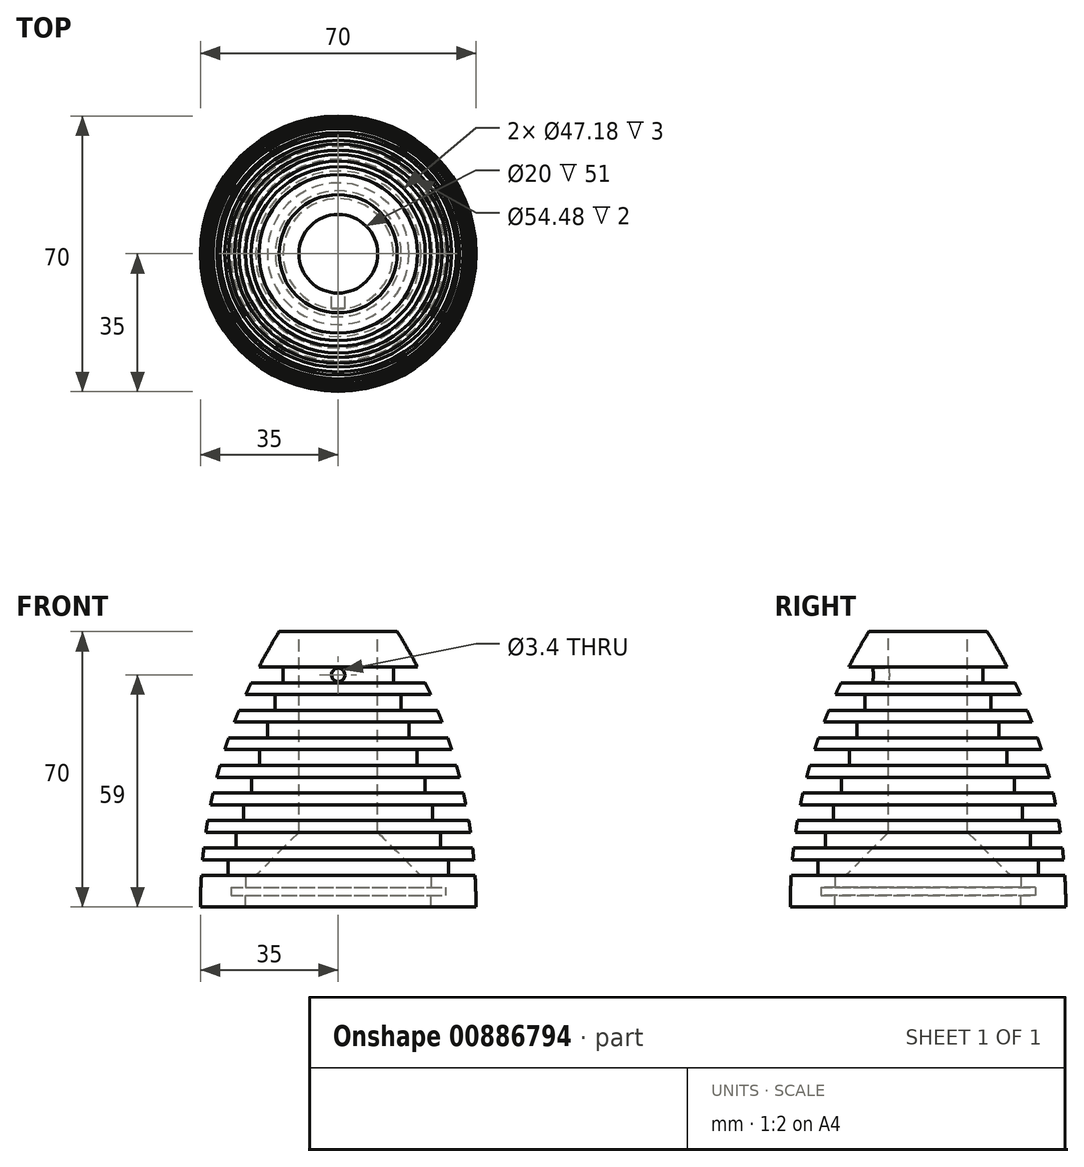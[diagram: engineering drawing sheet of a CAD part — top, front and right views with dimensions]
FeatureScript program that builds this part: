
annotation { "Feature Type Name" : "Feature", "Feature Type Description" : "" }
export const myFeature = defineFeature(function(context is Context, id is Id, definition is map)
    precondition{}
    {
        {
            var Q0;
            Q0=qCreatedBy(makeId("Front.planeOp"),FACE);
            var sketch = newSketch(context, id + "F0", { "sketchPlane" : qUnion([Q0])});
            skLineSegment(sketch, "E0", {"start": v(-35, -70) * mm, "end": v(-23.55, -70) * mm});
            skLineSegment(sketch, "E1", {"start": v(0, -70) * mm, "end": v(0, 0) * mm});
            skLineSegment(sketch, "E2", {"start": v(0, 0) * mm, "end": v(-15, 0) * mm});
            skArc(sketch, "E3", {"start": v(-15, 0) * mm, "mid": v(-17.65, -4.45) * mm, "end": v(-20.12, -9) * mm});
            skLineSegment(sketch, "E4", {"start": v(-23.5, -16) * mm, "end": v(-16, -16) * mm});
            skLineSegment(sketch, "E5", {"start": v(-16, -16) * mm, "end": v(-16, -20) * mm});
            skLineSegment(sketch, "E6", {"start": v(-16, -20) * mm, "end": v(-25.2, -20) * mm});
            skLineSegment(sketch, "E7", {"start": v(-26.38, -23) * mm, "end": v(-18, -23) * mm});
            skLineSegment(sketch, "E8", {"start": v(-18, -23) * mm, "end": v(-18, -27) * mm});
            skLineSegment(sketch, "E9", {"start": v(-18, -27) * mm, "end": v(-27.83, -27) * mm});
            skLineSegment(sketch, "E10", {"start": v(-28.82, -30) * mm, "end": v(-20, -30) * mm});
            skLineSegment(sketch, "E11", {"start": v(-20, -30) * mm, "end": v(-20, -34) * mm});
            skLineSegment(sketch, "E12", {"start": v(-20, -34) * mm, "end": v(-30.02, -34) * mm});
            skArc(sketch, "E13.trimOffspring", {"start": v(-25.2, -20) * mm, "mid": v(-25.8, -21.5) * mm, "end": v(-26.38, -23) * mm});
            skArc(sketch, "E14.trimOffspring", {"start": v(-27.83, -27) * mm, "mid": v(-28.33, -28.5) * mm, "end": v(-28.82, -30) * mm});
            skArc(sketch, "E15.trimOffspring", {"start": v(-30.02, -34) * mm, "mid": v(-30.43, -35.5) * mm, "end": v(-30.82, -37) * mm});
            skLineSegment(sketch, "E16", {"start": v(-30.82, -37) * mm, "end": v(-22, -37) * mm});
            skLineSegment(sketch, "E17", {"start": v(-22, -37) * mm, "end": v(-22, -41) * mm});
            skLineSegment(sketch, "E18", {"start": v(-22, -41) * mm, "end": v(-31.79, -41) * mm});
            skLineSegment(sketch, "E19", {"start": v(-32.42, -44) * mm, "end": v(-24, -44) * mm});
            skLineSegment(sketch, "E20", {"start": v(-24, -44) * mm, "end": v(-24, -48) * mm});
            skLineSegment(sketch, "E21", {"start": v(-24, -48) * mm, "end": v(-33.16, -48) * mm});
            skLineSegment(sketch, "E22", {"start": v(-33.63, -51) * mm, "end": v(-26, -51) * mm});
            skLineSegment(sketch, "E23", {"start": v(-26, -51) * mm, "end": v(-26, -55) * mm});
            skLineSegment(sketch, "E24", {"start": v(-26, -55) * mm, "end": v(-34.15, -55) * mm});
            skLineSegment(sketch, "E25", {"start": v(-34.46, -58) * mm, "end": v(-28, -58) * mm});
            skLineSegment(sketch, "E26", {"start": v(-28, -58) * mm, "end": v(-28, -62) * mm});
            skLineSegment(sketch, "E27", {"start": v(-28, -62) * mm, "end": v(-34.76, -62) * mm});
            skArc(sketch, "E28.trimOffspring", {"start": v(-31.79, -41) * mm, "mid": v(-32.11, -42.5) * mm, "end": v(-32.42, -44) * mm});
            skArc(sketch, "E29.trimOffspring", {"start": v(-33.16, -48) * mm, "mid": v(-33.4, -49.5) * mm, "end": v(-33.63, -51) * mm});
            skArc(sketch, "E30.trimOffspring", {"start": v(-34.15, -55) * mm, "mid": v(-34.31, -56.5) * mm, "end": v(-34.46, -58) * mm});
            skArc(sketch, "E31.trimOffspring", {"start": v(-34.76, -62) * mm, "mid": v(-34.94, -66) * mm, "end": v(-35, -70) * mm});
            skLineSegment(sketch, "E32", {"start": v(-20.12, -9) * mm, "end": v(-14, -9) * mm});
            skLineSegment(sketch, "E33", {"start": v(-14, -9) * mm, "end": v(-14, -13) * mm});
            skLineSegment(sketch, "E34", {"start": v(-14, -13) * mm, "end": v(-22.11, -13) * mm});
            skArc(sketch, "E35.trimOffspring", {"start": v(-22.11, -13) * mm, "mid": v(-22.81, -14.5) * mm, "end": v(-23.5, -16) * mm});
            skLineSegment(sketch, "E36", {"start": v(-23.55, -70) * mm, "end": v(-23.55, -67) * mm});
            skLineSegment(sketch, "E37", {"start": v(-23.55, -67) * mm, "end": v(-27.24, -67) * mm});
            skLineSegment(sketch, "E38", {"start": v(-27.24, -67) * mm, "end": v(-27.24, -65) * mm});
            skLineSegment(sketch, "E39", {"start": v(-27.24, -65) * mm, "end": v(-23.59, -65) * mm});
            skLineSegment(sketch, "E40", {"start": v(-23.59, -65) * mm, "end": v(-23.59, -62) * mm});
            skLineSegment(sketch, "E41", {"start": v(-23.59, -62) * mm, "end": v(0, -62) * mm});
            skSolve(sketch);
        }
        {
            var Q0;
            Q0 = qSketchRegion(id + "F0", true);
            var Q1;
            Q1=sQuery(id+"F0.wireOp",EDGE,"E1");
            revolve(context, id + "F1", {"surfaceOperationType" : NewSurfaceOperationType.NEW, "entities" : qUnion([Q0]), "axis" : qUnion([Q1]), "revolveType" : RevolveType.FULL});
        }
        {
            var Q0;
            Q0=qCreatedBy(makeId("Top.planeOp"),FACE);
            var sketch = newSketch(context, id + "F2", { "sketchPlane" : qUnion([Q0])});
            skCircle(sketch, "E42", {"center": v(0, 0) * mm, "radius": 10 * mm});
            skSolve(sketch);
        }
        {
            var Q0;
            Q0 = qSketchRegion(id + "F2", true);
            var Q1;
            Q1=makeQuery(id+"F1.opRevolve","SWEPT_FACE",FACE,{"disambiguationData":[OSD([sQuery(id+"F0.wireOp",EDGE,"E41")])]});
            var Q2;
            Q2=makeQuery(id+"F1.opRevolve","SWEPT_FACE",FACE,{"disambiguationData":[OSD([sQuery(id+"F0.wireOp",EDGE,"E41")])]});
            extrude(context, id + "F3", {"entities" : qUnion([Q0, Q1]), "operationType" : NewBodyOperationType.REMOVE, "endBound" : BoundingType.THROUGH_ALL, "oppositeDirection" : true, "depth" : 25 * mm, "endBoundEntityFace" : qUnion([Q2]), "offsetDistance" : 25 * mm});
        }
        {
            var Q0;
            Q0=qCreatedBy(makeId("Front.planeOp"),FACE);
            var sketch = newSketch(context, id + "F4", { "sketchPlane" : qUnion([Q0])});
            skCircle(sketch, "E43", {"center": v(0, -11) * mm, "radius": 1.7 * mm});
            skSolve(sketch);
        }
        {
            var Q0;
            Q0 = qSketchRegion(id + "F4", true);
            extrude(context, id + "F5", {"entities" : qUnion([Q0]), "operationType" : NewBodyOperationType.REMOVE, "depth" : 50 * mm, "offsetDistance" : 25 * mm});
        }
        {
            var Q0;
            {var subQ0=sQuery(id+"F0.wireOp",EDGE,"E41");Q0=makeQuery(id+"F3.boolean.opBoolean","INTERSECT",EDGE,{"derivedFrom":[makeQuery(id+"F1.opRevolve","SWEPT_FACE",FACE,{"disambiguationData":[OSD([subQ0])]}),makeQuery(id+"F3.opExtrude","CAP_FACE",FACE,{"disambiguationData":[OSD([subQ0])],"isStart":true}),makeQuery(id+"F3.opExtrude","SWEPT_FACE",FACE,{"disambiguationData":[OSD([sQuery(id+"F2.wireOp",EDGE,"E42")])]})]});}
            chamfer(context, id + "F6", {"entities" : qUnion([Q0]), "width" : 11 * mm, "tangentPropagation" : true});
        }
    });
